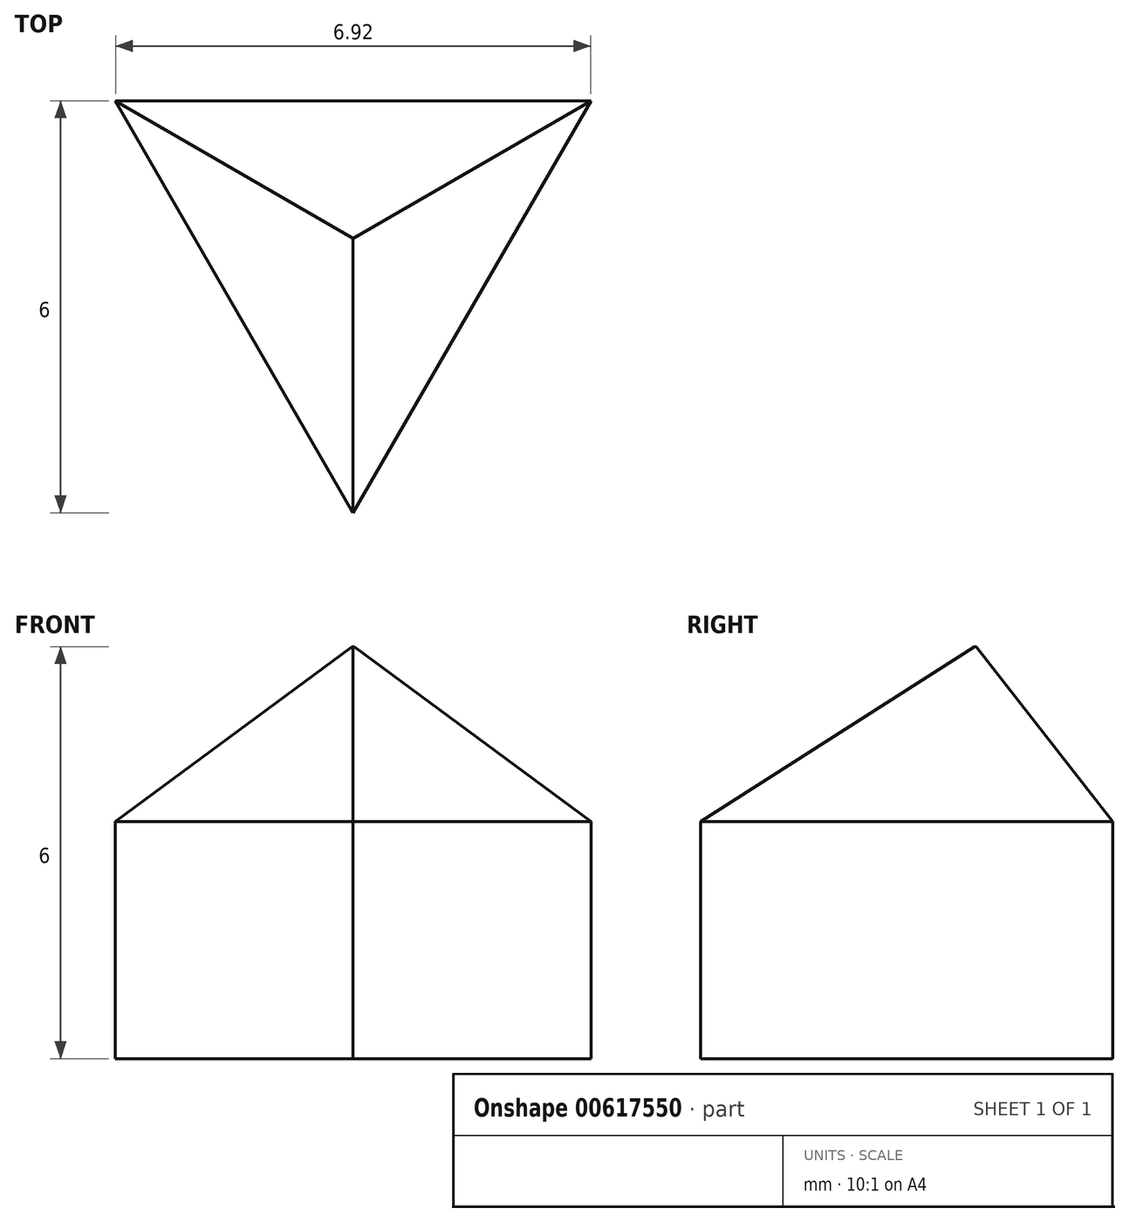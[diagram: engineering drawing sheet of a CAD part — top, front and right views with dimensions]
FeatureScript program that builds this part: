
annotation { "Feature Type Name" : "Feature", "Feature Type Description" : "" }
export const myFeature = defineFeature(function(context is Context, id is Id, definition is map)
    precondition{}
    {
        {
            var Q0;
            Q0=qCreatedBy(makeId("Top.planeOp"),FACE);
            var sketch = newSketch(context, id + "F0", { "sketchPlane" : qUnion([Q0])});
            skCircle(sketch, "E0.cCircle", {"center": v(0, 0) * mm, "radius": 2 * mm, "construction": true});
            skLineSegment(sketch, "E0.0", {"start": v(-3.46, 2) * mm, "end": v(3.46, 2) * mm});
            skLineSegment(sketch, "E0.1", {"start": v(3.46, 2) * mm, "end": v(0, -4) * mm});
            skLineSegment(sketch, "E0.2", {"start": v(0, -4) * mm, "end": v(-3.46, 2) * mm});
            skPoint(sketch, "E0.0.midPoint", {"position": v(0, 2) * mm});
            skSolve(sketch);
        }
        {
            var Q0;
            Q0 = qSketchRegion(id + "F0", true);
            extrude(context, id + "F1", {"entities" : qUnion([Q0]), "depth" : 6 * mm, "offsetDistance" : 25 * mm});
        }
        {
            var Q0;
            Q0=makeQuery(id+"F1.opExtrude","CAP_EDGE",EDGE,{"disambiguationData":[OSD([sQuery(id+"F0.wireOp",EDGE,"E0.1")])],"isStart":false});
            var Q1;
            Q1=makeQuery(id+"F1.opExtrude","CAP_EDGE",EDGE,{"disambiguationData":[OSD([sQuery(id+"F0.wireOp",EDGE,"E0.2")])],"isStart":false});
            var Q2;
            Q2=makeQuery(id+"F1.opExtrude","CAP_EDGE",EDGE,{"disambiguationData":[OSD([sQuery(id+"F0.wireOp",EDGE,"E0.0")])],"isStart":false});
            chamfer(context, id + "F2", {"entities" : qUnion([Q0, Q1, Q2]), "chamferType" : ChamferType.OFFSET_ANGLE, "width" : 2.55 * mm, "oppositeDirection" : false, "angle" : 38 * degree, "tangentPropagation" : true});
        }
    });
